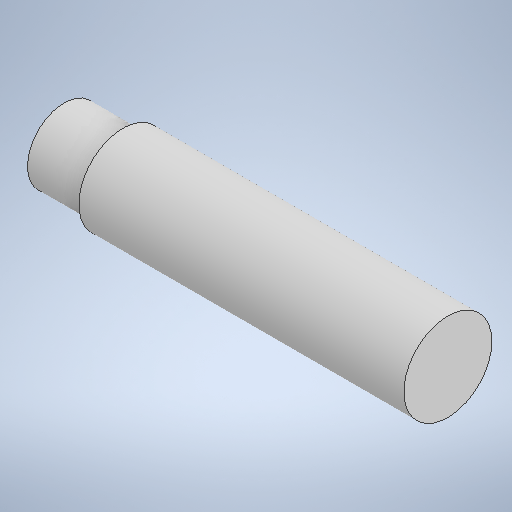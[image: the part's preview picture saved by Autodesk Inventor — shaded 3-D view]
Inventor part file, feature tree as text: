
AUTODESK INVENTOR PART (.ipt)
format: ipt  version: 2025.1 (Build 291241000, 241)  size: 243,712 bytes
history: native  units: mm
features: sketch x2, revolve x1, projected_geometry x1
ambient origin geometry x8: Origin, YZ Plane, XZ Plane, XY Plane, X Axis, Y Axis, Z Axis, Center Point
bodies: Solid1 (feature_tree)
feature tree (4):
  revolve  "Revolution1"  [1 undecoded]
  sketch  "Sketch3"  dims[d3=6.0mm d4=90.0deg d6=22.16mm]
  sketch  "Sketch1"  dims[d0=4.0mm d2=5.0mm]
  projected_geometry  "Projected Loop1"
note: 1 required parameter value undecoded (feature->parameter linkage not recoverable at this tier; creation-order binding heuristic only, values carry confidence <= 0.55)
